# Revit family: Spannklaue
name_source: partatom
category: HLS-Bauteile
revit_build: Autodesk Revit 2017 (Build: 20190507_1515(x64)
units: mm (PartAtom-declared; Revit-internal decimal feet)

## family parameters
Arbeitsebenenbasiert = Ja
Beim Laden mit Abzugskörper schneiden = Nein
Bemaßung runder Anschluss = Durchmesser verwenden
Gemeinsam genutzt = Ja
Immer vertikal = Nein
Raumberechnungspunkt = Nein
Teiletyp = Normal

## types (3) — shared parameters
Fabrikat = MEFA
Firma = MEFA Befestigungs- und Montagesysteme GmbH
Höhe = 28 mm
L = 73 mm
Länge = 74 mm  [stored 0.242782 ft]
Material = Stahl
Oberflaeche = galvanisch verzinkt
Profil = C-Profil
Stärke = 8 mm  [stored 0.0262467 ft]
Vorgabe-Ansicht = 1219 mm
zero-valued in all types: Höhe Profil

## per-type parameters (varying)
| type | Artikelnummer | B | B1 | Breite | D | EAN | Gewicht | Gewicht pro Bauteil | Kurztext1 | Kurztext2 | Langloch | Lochdurchmesser | Profiltyp | für Gewinde | max. zul. Last |
| Spannklaue M10 | 0814591 | 35 mm  [stored 0.114829 ft] | 12 mm  [stored 0.0393701 ft] | 35 mm  [stored 0.114829 ft] | 18 mm  [stored 0.0590551 ft] | 4250928420060 | 0.17 kg | 0.17 kg | Spannklaue C-Profil 35 | für Gewindestift M10 | 12 x 18 mm |  | 35 | M10 | 6.70 kN |
| Spannklaue M12 | 0816515 | 50 mm  [stored 0.164042 ft] | 14 mm  [stored 0.0459318 ft] | 50 mm  [stored 0.164042 ft] | 18 mm  [stored 0.0590551 ft] | 4250928420350 | 0.25 kg | 0.25 kg | Spannklaue C-Profil 45 | für Gewindestift M12 | 14 x 18 mm |  | 45 | M12 | 8.20 kN |
| Spannklaue M16 | 0819519 | 50 mm  [stored 0.164042 ft] | 18 mm  [stored 0.0590551 ft] | 50 mm  [stored 0.164042 ft] | 19 mm | 4250928420664 | 0.24 kg | 0.24 kg | Spannklaue C-Profil 45 | für Gewindestift M16 |  | 18 mm | 45 | M16 | 11.90 kN |

note: [stored X ft] marks values corroborated as IEEE doubles in the binary element streams (Revit-internal decimal feet)
